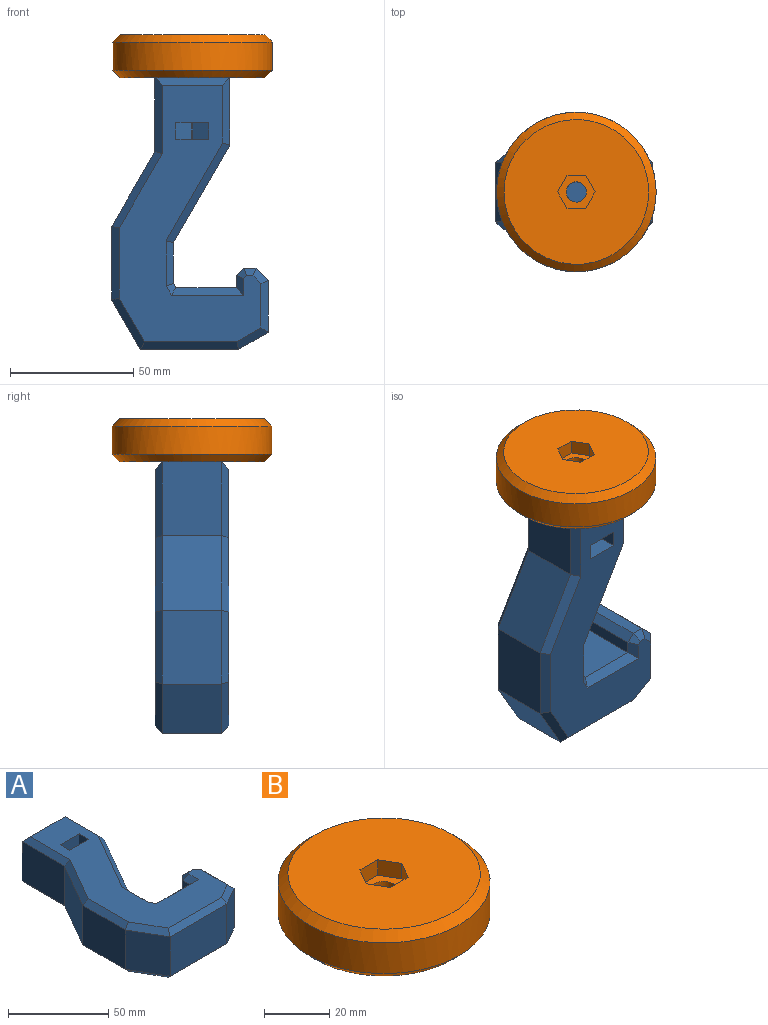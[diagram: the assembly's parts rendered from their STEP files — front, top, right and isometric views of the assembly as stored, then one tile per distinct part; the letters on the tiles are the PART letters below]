
ASSEMBLY  parts=2 mates=1
PART A: 63 faces, bbox 63.5x110.3x30 mm
  f0: plane 104.31x57.55mm, normal (0,0,1), area 2801.1mm2, adj f19,f20,f21,f22,f23,f24,f25,f26
  f1: plane 24x16.6mm, normal (1,0,0), area 398.5mm2, adj f2,f17,f28,f45
  f2: plane 39.66x24mm, normal (0.87,-0.5,0), area 1099.2mm2, adj f1,f3,f26,f43
  f3: plane 27.35x24mm, normal (1,0,0), area 656.3mm2, adj f2,f4,f24,f41
  f4: plane 30.4x24mm, normal (0,1,0), area 675.5mm2, adj f3,f5,f22,f39,f60
  f5: plane 30x24mm, normal (-1,0,0), area 720mm2, adj f4,f6,f20,f37
  f6: plane 30.31x24mm, normal (-0.87,0.5,0), area 840mm2, adj f5,f7,f19,f36
  f7: plane 30x24mm, normal (-1,0,0), area 720mm2, adj f6,f8,f21,f38
  f8: plane 24x20mm, normal (-0.87,-0.5,0), area 554.3mm2, adj f7,f9,f23,f40
  f9: plane 40x24mm, normal (0,-1,0), area 960mm2, adj f8,f10,f25,f42
  f10: plane 24x12mm, normal (0.5,-0.87,0), area 332.6mm2, adj f9,f11,f27,f44
  f11: plane 24x21.07mm, normal (1,0,0), area 505.7mm2, adj f10,f12,f29,f46
  f12: plane 24x5mm, normal (0.71,0.71,0), area 169.7mm2, adj f11,f13,f31,f48
  f13: plane 24x5mm, normal (0,1,0), area 120mm2, adj f12,f14,f33,f50
  f14: plane 24x3mm, normal (-0.71,0.71,0), area 101.8mm2, adj f13,f15,f35,f52
  f15: plane 24x5mm, normal (-1,0,0), area 120mm2, adj f14,f16,f34,f51
  f16: plane 24.57x24mm, normal (0,1,0), area 589.6mm2, adj f15,f17,f32,f49
  f17: plane 24x1.7mm, normal (0.87,0.5,0), area 47.1mm2, adj f1,f16,f30,f47
  f18: plane 104.31x57.55mm, normal (0,0,-1), area 2890.9mm2, adj f36,f37,f38,f39,f40,f41,f42,f43
  f19: plane 31.11x20.5mm, normal (-0.61,0.35,0.71), area 148.5mm2, adj f0,f6,f20,f21
  f20: plane 30.8x3mm, normal (-0.71,0,0.71), area 122.6mm2, adj f0,f5,f19,f22
  f21: plane 30x3mm, normal (-0.71,0,0.71), area 123.9mm2, adj f0,f7,f19,f23
  f22: plane 30.4x3mm, normal (0,0.71,0.71), area 116.2mm2, adj f0,f4,f20,f24
  f23: plane 20.8x13.28mm, normal (-0.61,-0.35,0.71), area 92.6mm2, adj f0,f8,f21,f25
  f24: plane 27.35x3mm, normal (0.71,0,0.71), area 107.9mm2, adj f0,f3,f22,f26
  f25: plane 40x3mm, normal (0,-0.71,0.71), area 164.3mm2, adj f0,f9,f23,f27
  f26: plane 40.47x25.9mm, normal (0.61,-0.35,0.71), area 194.3mm2, adj f0,f2,f24,f28
  f27: plane 12.8x8.66mm, normal (0.35,-0.61,0.71), area 53.4mm2, adj f0,f10,f25,f29
  f28: plane 18.21x3mm, normal (0.71,0,0.71), area 73.8mm2, adj f0,f1,f26,f30
  f29: plane 21.07x3mm, normal (0.71,0,0.71), area 83.1mm2, adj f0,f11,f27,f31
  f30: plane 4.7x3.98mm, normal (0.61,0.35,0.71), area 13.7mm2, adj f0,f17,f28,f32
  f31: plane 6.24x6.24mm, normal (0.5,0.5,0.71), area 24.7mm2, adj f0,f12,f29,f33
  f32: plane 29.3x3mm, normal (0,0.71,0.71), area 114.3mm2, adj f0,f16,f30,f34
  f33: plane 5x3mm, normal (0,0.71,0.71), area 15.9mm2, adj f0,f13,f31,f35
  f34: plane 8x3mm, normal (-0.71,0,0.71), area 24.9mm2, adj f0,f15,f32,f35
  f35: plane 4.24x4.24mm, normal (-0.5,0.5,0.71), area 12.7mm2, adj f0,f14,f33,f34
  f36: plane 31.11x20.5mm, normal (-0.61,0.35,-0.71), area 148.5mm2, adj f6,f18,f37,f38
  f37: plane 30.8x3mm, normal (-0.71,0,-0.71), area 122.6mm2, adj f5,f18,f36,f39
  f38: plane 30x3mm, normal (-0.71,0,-0.71), area 123.9mm2, adj f7,f18,f36,f40
  f39: plane 30.4x3mm, normal (0,0.71,-0.71), area 116.2mm2, adj f4,f18,f37,f41
  f40: plane 20.8x13.28mm, normal (-0.61,-0.35,-0.71), area 92.6mm2, adj f8,f18,f38,f42
  f41: plane 27.35x3mm, normal (0.71,0,-0.71), area 107.9mm2, adj f3,f18,f39,f43
  f42: plane 40x3mm, normal (0,-0.71,-0.71), area 164.3mm2, adj f9,f18,f40,f44
  f43: plane 40.47x25.9mm, normal (0.61,-0.35,-0.71), area 194.3mm2, adj f2,f18,f41,f45
  f44: plane 12.8x8.66mm, normal (0.35,-0.61,-0.71), area 53.4mm2, adj f10,f18,f42,f46
  f45: plane 18.21x3mm, normal (0.71,0,-0.71), area 73.8mm2, adj f1,f18,f43,f47
  f46: plane 21.07x3mm, normal (0.71,0,-0.71), area 83.1mm2, adj f11,f18,f44,f48
  f47: plane 4.7x3.98mm, normal (0.61,0.35,-0.71), area 13.7mm2, adj f17,f18,f45,f49
  f48: plane 6.24x6.24mm, normal (0.5,0.5,-0.71), area 24.7mm2, adj f12,f18,f46,f50
  f49: plane 29.3x3mm, normal (0,0.71,-0.71), area 114.3mm2, adj f16,f18,f47,f51
  f50: plane 5x3mm, normal (0,0.71,-0.71), area 15.9mm2, adj f13,f18,f48,f52
  f51: plane 8x3mm, normal (-0.71,0,-0.71), area 24.9mm2, adj f15,f18,f49,f52
  f52: plane 4.24x4.24mm, normal (-0.5,0.5,-0.71), area 12.7mm2, adj f14,f18,f50,f51
  f53: plane 22.3x13.4mm, normal (0,1,0), area 220.3mm2, adj f0,f54,f56,f57,f58,f59,f61
  f54: plane 18.55x6.7mm, normal (-1,0,0), area 124.3mm2, adj f0,f53,f55,f59
  f55: plane 22.3x13.4mm, normal (0,-1,0), area 220.3mm2, adj f0,f54,f56,f57,f58,f59,f60
  f56: plane 18.55x6.7mm, normal (1,0,0), area 124.3mm2, adj f0,f53,f55,f58
  f57: plane 6.7x0.4mm, normal (0,0,1), area 2.7mm2, adj f53,f55,f58,f59
  f58: plane 6.7x6.5mm, normal (0.5,0,0.87), area 50.3mm2, adj f53,f55,f56,f57
  f59: plane 6.7x6.5mm, normal (-0.5,0,0.87), area 50.3mm2, adj f53,f54,f55,f57
  f60: cylinder r=4.15mm len=18.3mm, axis (0,1,0), area 477.2mm2, adj f4,f55
  f61: cylinder r=4.15mm len=8.3mm, axis (0,1,0), area 80.8mm2, adj f53,f62
  f62: plane 8.3x8.3mm, normal (0,1,0), area 54.1mm2, adj f61
PART B: 13 faces, bbox 64.8x64.8x17.5 mm
  f0: cylinder r=4.1mm len=11.7mm, axis (0,0,1), area 301.4mm2, adj f3,f10
  f1: plane 58.8x58.8mm, normal (0,0,1), area 2564.6mm2, adj f4,f5,f6,f7,f8,f9,f12
  f2: cylinder r=32.4mm len=64.8mm, axis (0,0,1), area 2341.1mm2, adj f11,f12
  f3: plane 58.8x58.8mm, normal (0,0,-1), area 2662.7mm2, adj f0,f11
  f4: plane 6.6x5.8mm, normal (-0.87,-0.5,0), area 44.2mm2, adj f1,f5,f9,f10
  f5: plane 7.62x5.8mm, normal (0,-1,0), area 44.2mm2, adj f1,f4,f6,f10
  f6: plane 6.6x5.8mm, normal (0.87,-0.5,0), area 44.2mm2, adj f1,f5,f7,f10
  f7: plane 6.6x5.8mm, normal (0.87,0.5,0), area 44.2mm2, adj f1,f6,f8,f10
  f8: plane 7.62x5.8mm, normal (0,1,0), area 44.2mm2, adj f1,f7,f9,f10
  f9: plane 6.6x5.8mm, normal (-0.87,0.5,0), area 44.2mm2, adj f1,f4,f8,f10
  f10: plane 15.24x13.2mm, normal (0,0,1), area 98.1mm2, adj f0,f4,f5,f6,f7,f8,f9
  f11: cone r=32.4mm half-angle=45deg, axis (0,0,1), area 823.7mm2, adj f2,f3
  f12: cone r=29.4mm half-angle=45deg, axis (0,0,-1), area 823.7mm2, adj f1,f2
PLACE A rot(axis=(1,0,0),90deg) t=(-51.72,10.31,-98.7)mm
PLACE B t=(-51.72,10.31,-98.7)mm
MATE planar A.f60 <-> B.f0  axis (0,0,1) through (-51.72,10.31,-98.7)mm
